# Revit family: WD18_Down
name_source: partatom
category: Lighting Fixtures
revit_build: Autodesk Revit 2013 (Build: 20130531_2115(x64)
units: mm (PartAtom-declared; Revit-internal decimal feet)

## types (1)
- WD18 - Down
    Apparent Load = 0 VA
    Assembly Code = D5020200
    Color Filter = 16777215
    Default Elevation = 80"
    Description = Wall Mounted Luminaire
    Dimming Lamp Color Temperature Shift = <None>
    Emit Shape Visible in Rendering = No
    Emit from Rectangle Length = 15"
    Emit from Rectangle Width = 15"
    Finish = All colors shall be a Super TGIC powder coat paint. Optional white (WH) and custom colors available.
    Full Load Current = 0 A
    Glass Material = Glass-Kim Lighting-Clear
    Housing material = Metal-Kim Lighting-Spun Aluminum
    Lamp = 120 LEDs
    Load Classification = Lighting
    Manufacturer = Kim Lighting
    Manufacturer Fax = 626-369-2695
    MasterFormat Title = Parking Lighting, Site Lighting
    Model = WD18 - Down
    Note Text = LF
    Note Visible = Yes
    Number of Poles = 1
    OmniClass Number = 23-80 70 14 11 17
    OmniClass Title = Wall or Ceiling Mounted External Lighting
    Photometric Notes = More IES files download on Photometric Web Link
    Photometric Web File = wd18d3-400mc.ies
    Photometric Web Link = http://www.kimlighting.com
    Power Factor = 1
    Product Documentation Link = http://www.kimlighting.com
    Product Page URL = http://www.kimlighting.com
    Revision Date = 11/07/2017
    Series = Wall Director
    Tilt Angle = 90.00°
    Type Comments = Lighting Fixture
    URL = www.kimlighting.com/
    Voltage = 120 V
    Wattage Comments = 127W

## geometry (parser evidence)
native form markers: Sweep x1
no freeform markers — native parametric forms only
